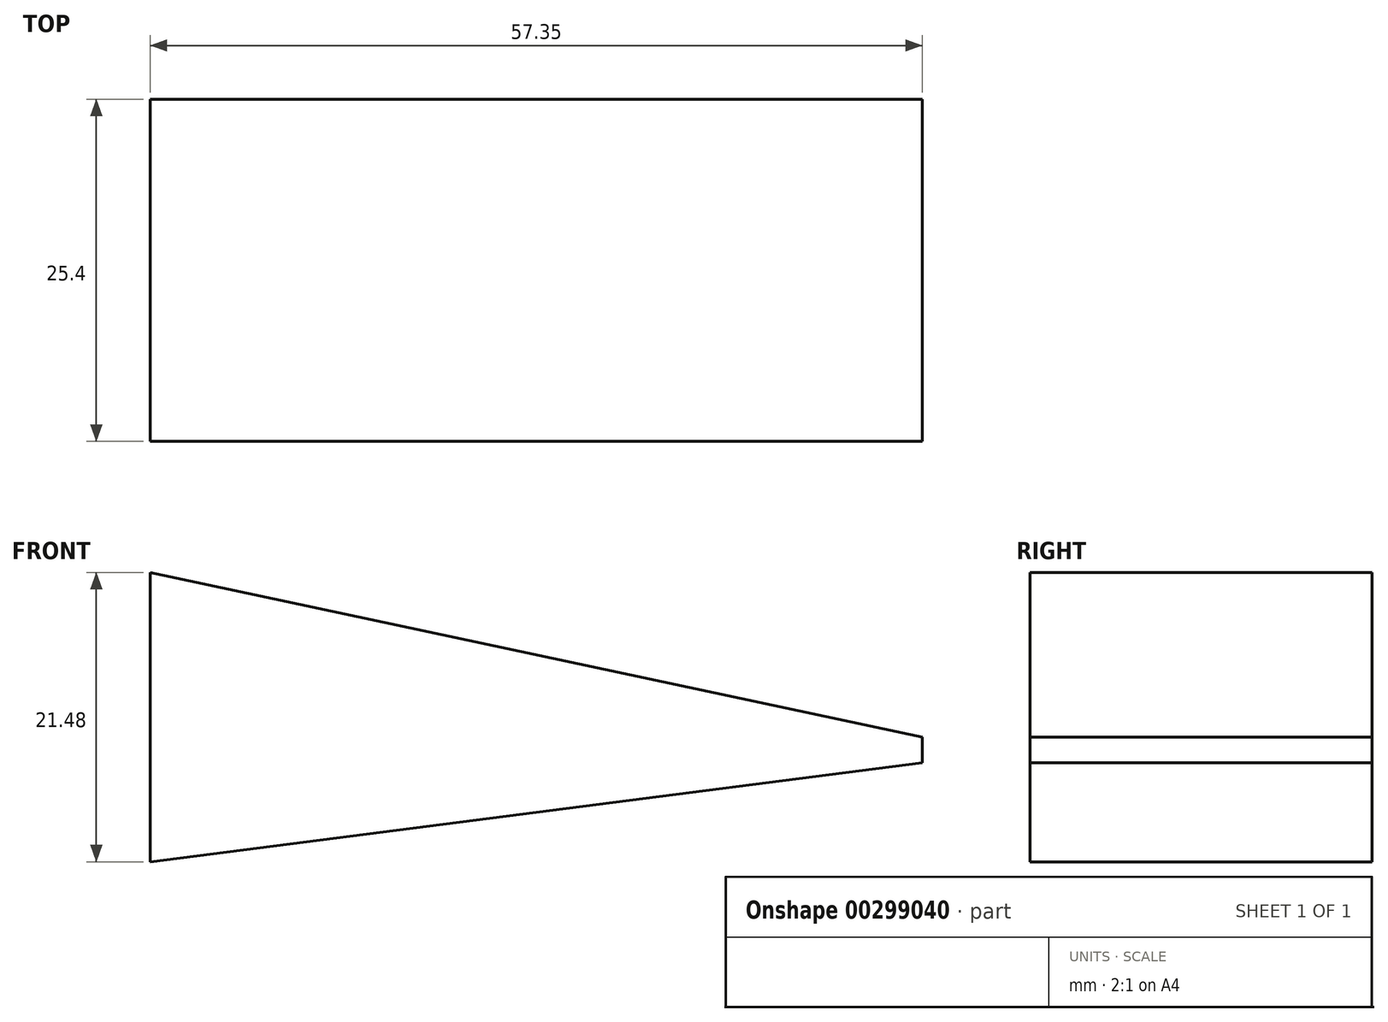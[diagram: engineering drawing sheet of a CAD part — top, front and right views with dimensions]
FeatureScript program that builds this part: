
annotation { "Feature Type Name" : "Feature", "Feature Type Description" : "" }
export const myFeature = defineFeature(function(context is Context, id is Id, definition is map)
    precondition{}
    {
        {
            var Q0;
            Q0=qCreatedBy(makeId("Front.planeOp"),FACE);
            var sketch = newSketch(context, id + "F0", { "sketchPlane" : qUnion([Q0])});
            skLineSegment(sketch, "E0.bottom", {"start": v(0, 33.9) * mm, "end": v(57.35, 33.9) * mm});
            skLineSegment(sketch, "E0.top", {"start": v(0, 12.42) * mm, "end": v(57.35, 12.42) * mm});
            skLineSegment(sketch, "E0.left", {"start": v(0, 33.9) * mm, "end": v(0, 12.42) * mm});
            skLineSegment(sketch, "E0.right", {"start": v(57.35, 33.9) * mm, "end": v(57.35, 12.42) * mm});
            skSolve(sketch);
        }
        {
            var Q0;
            Q0=makeQuery(id+"F0.imprint","IMPRINT",FACE,{"disambiguationData":[TD([[makeQuery(id+"F0.imprint","IMPRINT",EDGE,{"derivedFrom":sQuery(id+"F0.wireOp",EDGE,"E0.bottom")}),-1.0]])]});
            extrude(context, id + "F1", {"entities" : qUnion([Q0]), "depth" : 25.4 * mm});
        }
        {
            var Q0;
            Q0=qCreatedBy(makeId("Front.planeOp"),FACE);
            var sketch = newSketch(context, id + "F2", { "sketchPlane" : qUnion([Q0])});
            skLineSegment(sketch, "E1.0", {"start": v(0, 33.9) * mm, "end": v(57.35, 33.9) * mm});
            skLineSegment(sketch, "E2.0", {"start": v(0, 33.9) * mm, "end": v(0, 12.42) * mm});
            skLineSegment(sketch, "E3.0", {"start": v(0, 12.42) * mm, "end": v(57.35, 12.42) * mm});
            skLineSegment(sketch, "E4.0", {"start": v(57.35, 33.9) * mm, "end": v(57.35, 12.42) * mm});
            skLineSegment(sketch, "E5", {"start": v(0, 33.9) * mm, "end": v(57.35, 21.69) * mm});
            skSolve(sketch);
        }
        {
            var Q0;
            {var subQ0=sQuery(id+"F2.wireOp",EDGE,"E1.0");Q0=makeQuery(id+"F2.imprint","IMPRINT",FACE,{"disambiguationData":[TD([[makeQuery(id+"F2.imprint","IMPRINT",EDGE,{"derivedFrom":subQ0}),-1.0]])]});}
            extrude(context, id + "F3", {"entities" : qUnion([Q0]), "operationType" : NewBodyOperationType.REMOVE, "depth" : 25.4 * mm});
        }
        {
            var Q0;
            Q0=qCreatedBy(makeId("Front.planeOp"),FACE);
            var sketch = newSketch(context, id + "F4", { "sketchPlane" : qUnion([Q0])});
            skLineSegment(sketch, "E6.0", {"start": v(0, 33.9) * mm, "end": v(57.35, 21.69) * mm});
            skLineSegment(sketch, "E7.0", {"start": v(0, 33.9) * mm, "end": v(0, 12.42) * mm});
            skLineSegment(sketch, "E8.0", {"start": v(57.35, 21.69) * mm, "end": v(57.35, 12.42) * mm});
            skLineSegment(sketch, "E9.0", {"start": v(0, 12.42) * mm, "end": v(57.35, 12.42) * mm});
            skLineSegment(sketch, "E10", {"start": v(57.35, 19.79) * mm, "end": v(0, 12.42) * mm});
            skSolve(sketch);
        }
        {
            var Q0;
            {var subQ0=sQuery(id+"F4.wireOp",EDGE,"E9.0");Q0=makeQuery(id+"F4.imprint","IMPRINT",FACE,{"disambiguationData":[TD([[makeQuery(id+"F4.imprint","IMPRINT",EDGE,{"derivedFrom":subQ0}),1.0]])]});}
            extrude(context, id + "F5", {"entities" : qUnion([Q0]), "operationType" : NewBodyOperationType.REMOVE, "depth" : 25.4 * mm});
        }
    });
